# Revit family: MixerSet_Basin_Nero_Mecca_Arc
name_source: partatom
category: Plumbing Fixtures
units: mm (PartAtom-declared; Revit-internal decimal feet)

## family parameters
Always vertical = Yes
Cut with Voids When Loaded = Yes
Maintain Annotation Orientation = No
OmniClass Number = 23.31.11.19
OmniClass Title = Faucet Mixing Valves
Part Type = Normal
Room Calculation Point = No
Round Connector Dimension = Use Diameter
Shared = No
Work Plane-Based = No

## types (7) — shared parameters
Assembly Code = D2010
CW Connection = Yes
Default Elevation = 900 mm  [stored 2.95276 ft]
HW Connection = Yes
IfcExportAs = IfcValve
IfcExportType = MIXING
Manufacturer = Nero
ManufacturerOverallDepth = 175 mm  [stored 0.574147 ft]
ManufacturerOverallHeight = 210 mm  [stored 0.688976 ft]
ManufacturerOverallWidth = 220 mm  [stored 0.721785 ft]
ModifiedIssue = 20251009 $
URL = https://nerotapware.com.au
Uniclass2015Code = Pr_40_20_87
Uniclass2015Title = Taps and water supply outlet fittings
Uniclass2015Version = Products v1.35
Vent Connection = No
Waste Connection = No
zero-valued in all types: CWFU, HWFU, WFU

## per-type parameters (varying)
| type | Description | ManufacturerSpecCode | Material | Model | Type Comments |
| Chrome (NR221901gCH) | Mecca Hob Baisn Mixer Set Arc Spout Chrome | NR221901gCH | Metal_Chrome_Nero | NR221901gCH | Mixer Set - Basin - Arc - Chrome |
| Matte Black (NR221901gMB) | Mecca Hob Baisn Mixer Set Arc Spout Matte Black | NR221901gMB | Metal_MatteBlack_Nero | NR221901gMB | Mixer Set - Basin - Arc - Matte Black |
| Brushed Nickel (NR221901gBN) | Mecca Hob Baisn Mixer Set Arc Spout Brushed Nickel | NR221901gBN | Metal_Nickel_Nero_Brushed | NR221901gBN | Mixer Set - Basin - Arc - Brushed Nickel |
| Gun Metal (NR221901gGM) | Mecca Hob Baisn Mixer Set Arc Spout Gun Metal | NR221901gGM | Metal_GunMetal_Nero | NR221901gGM | Mixer Set - Basin - Arc - Gun Metal |
| Brushed Gold (NR221901gBG) | Mecca Hob Baisn Mixer Set Arc Spout Brushed Gold | NR221901gBG | Metal_Gold_Nero_Brushed | NR221901gBG | Mixer Set - Basin - Arc - Brushed Gold |
| Brushed Bronze (NR221901gBZ) | Mecca Hob Baisn Mixer Set Arc Spout Brushed Bronze | NR221901gBZ | Metal_Bronze_Nero_Brushed | NR221901gBZ | Mixer Set - Basin - Arc - Brushed Bronze |
| Matte White (NR221901gMW) | Mecca Hob Baisn Mixer Set Arc Spout Matte White | NR221901gMW | Metal_MatteWhite_Nero | NR221901gMW | Mixer Set - Basin - Arc - Matte White |

note: [stored X ft] marks values corroborated as IEEE doubles in the binary element streams (Revit-internal decimal feet)

## geometry (parser evidence)
native form markers: Sweep x2
no freeform markers — native parametric forms only
